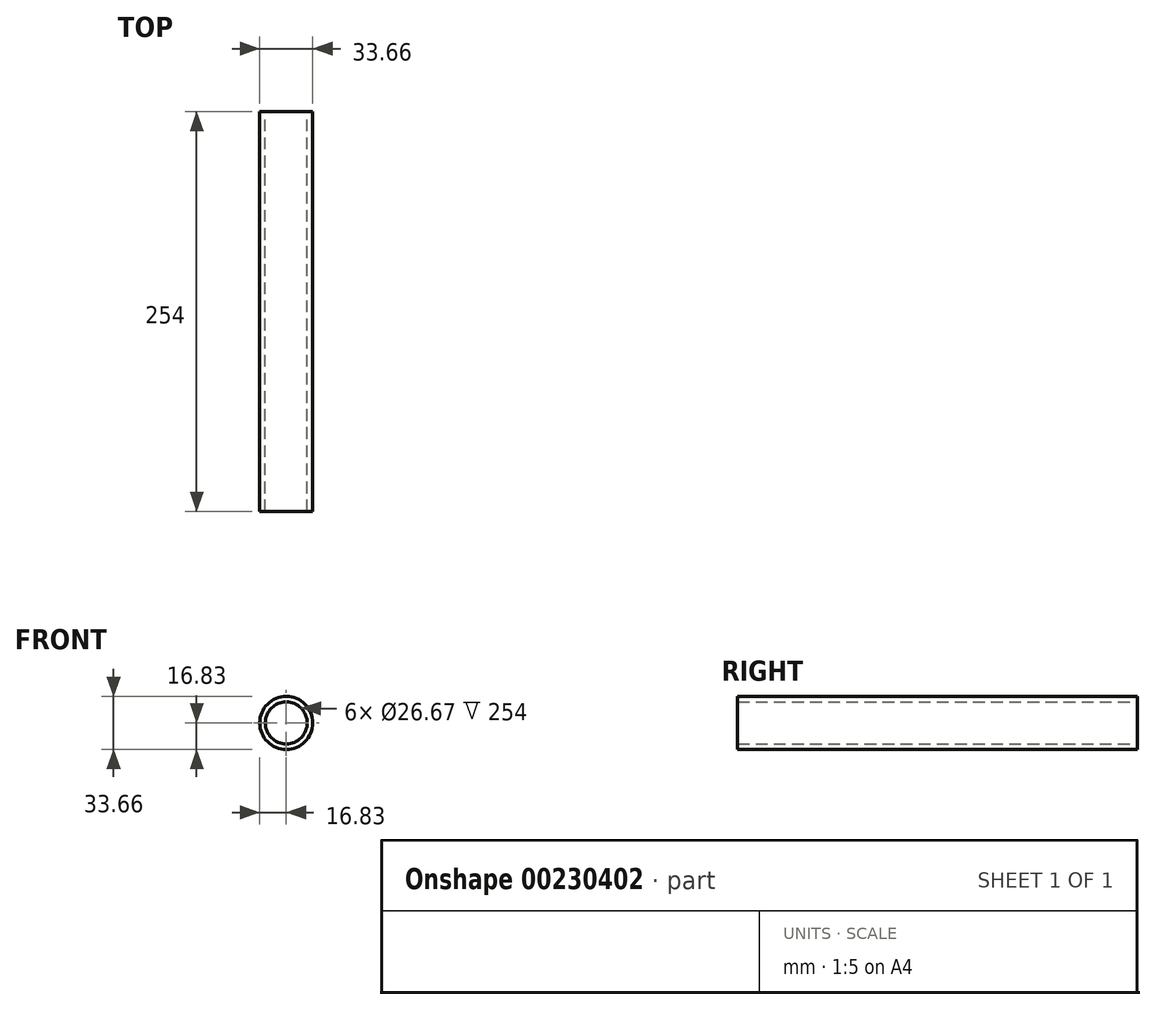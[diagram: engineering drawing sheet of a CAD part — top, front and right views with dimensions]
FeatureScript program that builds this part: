
annotation { "Feature Type Name" : "Feature", "Feature Type Description" : "" }
export const myFeature = defineFeature(function(context is Context, id is Id, definition is map)
    precondition{}
    {
        {
            var Q0;
            Q0=qCreatedBy(makeId("Front.planeOp"),FACE);
            var sketch = newSketch(context, id + "F0", { "sketchPlane" : qUnion([Q0])});
            skCircle(sketch, "E0", {"center": v(0, 0) * mm, "radius": 13.34 * mm});
            skCircle(sketch, "E1", {"center": v(0, 0) * mm, "radius": 16.83 * mm});
            skSolve(sketch);
        }
        {
            var Q0;
            Q0=qSketchRegion(id+"F0",true);
            extrude(context, id + "F1", {"entities" : qUnion([Q0]), "depth" : 254 * mm});
        }
    });
